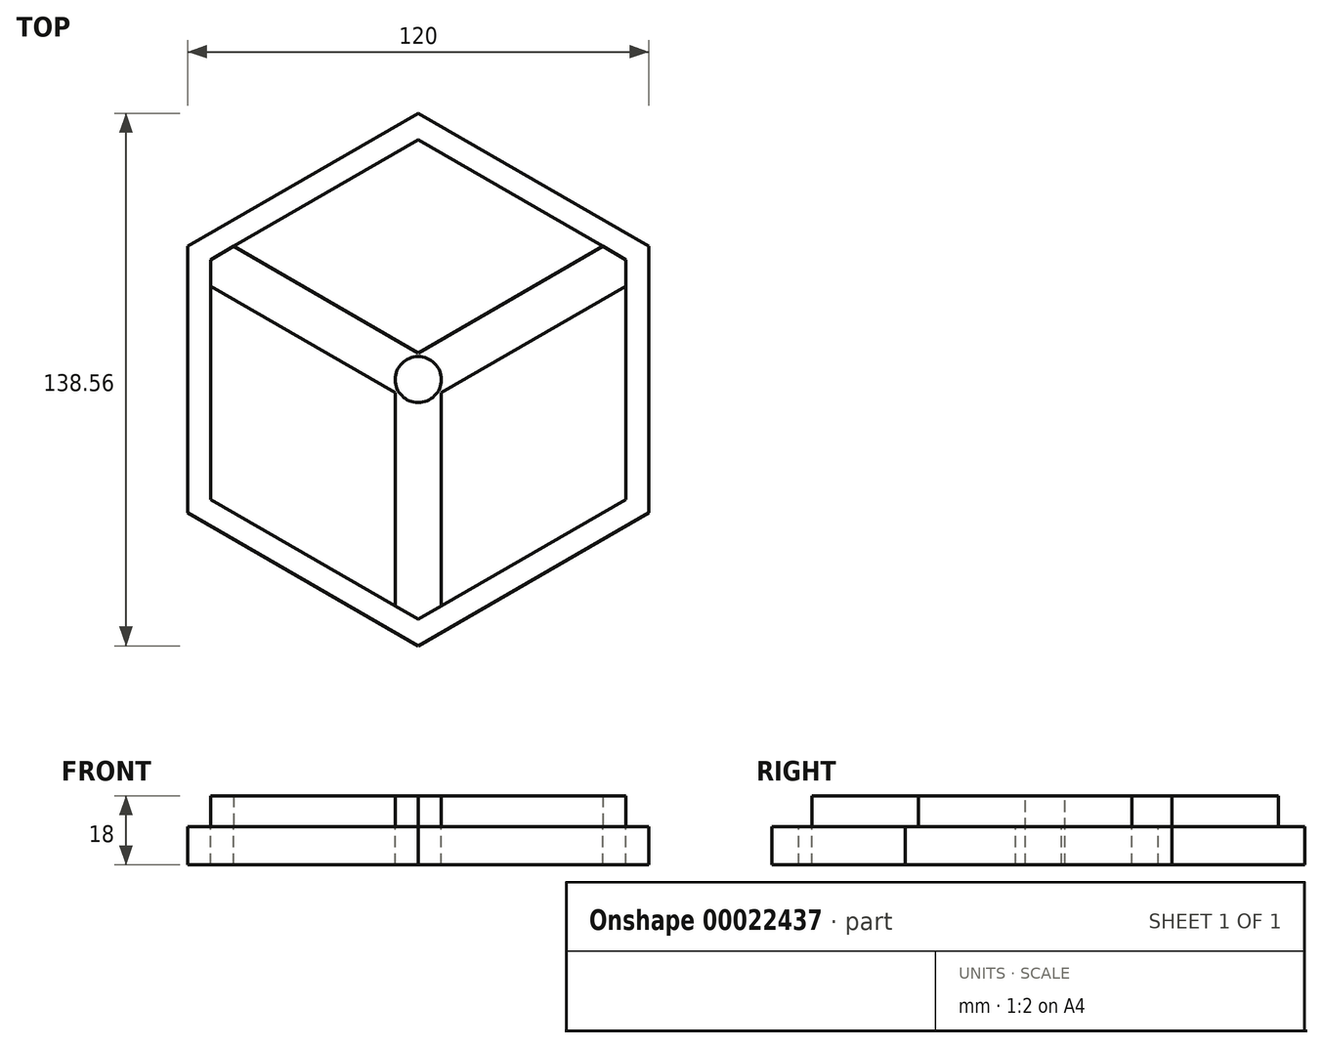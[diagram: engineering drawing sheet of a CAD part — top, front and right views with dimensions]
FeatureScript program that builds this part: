
annotation { "Feature Type Name" : "Feature", "Feature Type Description" : "" }
export const myFeature = defineFeature(function(context is Context, id is Id, definition is map)
    precondition{}
    {
        {
            var Q0;
            Q0=qCreatedBy(makeId("Top.planeOp"),FACE);
            var sketch = newSketch(context, id + "F0", { "sketchPlane" : qUnion([Q0])});
            skCircle(sketch, "E0.cCircle", {"center": v(0, 0) * mm, "radius": 60 * mm, "construction": true});
            skLineSegment(sketch, "E0.0", {"start": v(60, -34.64) * mm, "end": v(0, -69.28) * mm});
            skLineSegment(sketch, "E0.1", {"start": v(0, -69.28) * mm, "end": v(-60, -34.64) * mm});
            skLineSegment(sketch, "E0.2", {"start": v(-60, -34.64) * mm, "end": v(-60, 34.64) * mm});
            skLineSegment(sketch, "E0.3", {"start": v(-60, 34.64) * mm, "end": v(0, 69.28) * mm});
            skLineSegment(sketch, "E0.4", {"start": v(0, 69.28) * mm, "end": v(60, 34.64) * mm});
            skLineSegment(sketch, "E0.5", {"start": v(60, 34.64) * mm, "end": v(60, -34.64) * mm});
            skPoint(sketch, "E0.0.midPoint", {"position": v(30, -51.96) * mm});
            skCircle(sketch, "E1", {"center": v(0, 0) * mm, "radius": 30 * mm, "construction": true});
            skCircle(sketch, "E2", {"center": v(0, -69.28) * mm, "radius": 10 * mm, "construction": true});
            skCircle(sketch, "E3", {"center": v(60, 34.64) * mm, "radius": 10 * mm, "construction": true});
            skCircle(sketch, "E4", {"center": v(-60, 34.64) * mm, "radius": 10 * mm, "construction": true});
            skLineSegment(sketch, "E5.0", {"start": v(-54, -31.18) * mm, "end": v(-54, 31.18) * mm});
            skLineSegment(sketch, "E5.1", {"start": v(0, -62.35) * mm, "end": v(-54, -31.18) * mm});
            skLineSegment(sketch, "E5.2", {"start": v(54, -31.18) * mm, "end": v(0, -62.35) * mm});
            skLineSegment(sketch, "E5.3", {"start": v(54, 31.18) * mm, "end": v(54, -31.18) * mm});
            skLineSegment(sketch, "E5.4", {"start": v(0, 62.35) * mm, "end": v(54, 31.18) * mm});
            skLineSegment(sketch, "E5.5", {"start": v(-54, 31.18) * mm, "end": v(0, 62.35) * mm});
            skLineSegment(sketch, "E6", {"start": v(-54, 31.18) * mm, "end": v(0, 0) * mm});
            skLineSegment(sketch, "E7", {"start": v(0, 0) * mm, "end": v(54, 31.18) * mm});
            skLineSegment(sketch, "E8", {"start": v(0, 0) * mm, "end": v(0, -62.35) * mm});
            skArc(sketch, "E9.0.startCap", {"start": v(-57, 25.98) * mm, "mid": v(-59.2, 34.18) * mm, "end": v(-51, 36.37) * mm});
            skArc(sketch, "E9.0.endCap", {"start": v(3, 5.2) * mm, "mid": v(5.2, -3) * mm, "end": v(-3, -5.2) * mm});
            skLineSegment(sketch, "E9.0.left", {"start": v(-51, 36.37) * mm, "end": v(0, 6.93) * mm});
            skLineSegment(sketch, "E9.0.right", {"start": v(-57, 25.98) * mm, "end": v(-6, -3.46) * mm});
            skArc(sketch, "E9.1.startCap", {"start": v(3, -5.2) * mm, "mid": v(-5.2, -3) * mm, "end": v(-3, 5.2) * mm});
            skArc(sketch, "E9.1.endCap", {"start": v(51, 36.37) * mm, "mid": v(59.2, 34.18) * mm, "end": v(57, 25.98) * mm});
            skLineSegment(sketch, "E9.1.left", {"start": v(0, 6.93) * mm, "end": v(51, 36.37) * mm});
            skLineSegment(sketch, "E9.1.right", {"start": v(6, -3.46) * mm, "end": v(57, 25.98) * mm});
            skArc(sketch, "E9.2.startCap", {"start": v(-6, 0) * mm, "mid": v(0, 6) * mm, "end": v(6, 0) * mm});
            skArc(sketch, "E9.2.endCap", {"start": v(6, -62.35) * mm, "mid": v(0, -68.35) * mm, "end": v(-6, -62.35) * mm});
            skLineSegment(sketch, "E9.2.left", {"start": v(6, -3.46) * mm, "end": v(6, -62.35) * mm});
            skLineSegment(sketch, "E9.2.right", {"start": v(-6, -3.46) * mm, "end": v(-6, -62.35) * mm});
            skLineSegment(sketch, "E10", {"start": v(0, 0) * mm, "end": v(-60, -34.64) * mm, "construction": true});
            skLineSegment(sketch, "E11", {"start": v(0, 0) * mm, "end": v(60, -34.64) * mm, "construction": true});
            skLineSegment(sketch, "E12", {"start": v(-54, 24.25) * mm, "end": v(-6, -58.89) * mm, "construction": true});
            skLineSegment(sketch, "E13", {"start": v(54, 24.25) * mm, "end": v(6, -58.89) * mm, "construction": true});
            skLineSegment(sketch, "E14", {"start": v(-48, 34.64) * mm, "end": v(48, 34.64) * mm, "construction": true});
            skSolve(sketch);
        }
        {
            var Q0;
            Q0 = qSketchRegion(id + "F0", true);
            var Q1;
            {var subQ3=sQuery(id+"F0.wireOp",EDGE,"E9.0.startCap");Q1=makeQuery(id+"F0.imprint","IMPRINT",FACE,{"disambiguationData":[TD([[makeQuery(id+"F0.imprint","IMPRINT",EDGE,{"derivedFrom":subQ3}),-1.0]])]});}
            var Q2;
            {var subQ0=sQuery(id+"F0.wireOp",EDGE,"E9.2.startCap");var subQ2=makeQuery(id+"F0.imprint","IMPRINT",VERTEX,{"disambiguationData":[OD(0.0)],"derivedFrom":subQ0});Q2=makeQuery(id+"F0.imprint","IMPRINT",FACE,{"disambiguationData":[TD([[makeQuery(id+"F0.imprint","IMPRINT",EDGE,{"disambiguationData":[TD([[subQ2,-1.0]])],"derivedFrom":subQ0}),1.0]])]});}
            var Q3;
            {var subQ1=sQuery(id+"F0.wireOp",EDGE,"E5.1");var subQ5=sQuery(id+"F0.wireOp",EDGE,"E5.0");var subQ7=makeQuery(id+"F0.imprint","INTERSECT",VERTEX,{"derivedFrom":[subQ5,subQ1]});Q3=makeQuery(id+"F0.imprint","IMPRINT",FACE,{"disambiguationData":[TD([[makeQuery(id+"F0.imprint","IMPRINT",EDGE,{"disambiguationData":[TD([[subQ7,-1.0]])],"derivedFrom":subQ5}),-1.0]])]});}
            var Q4;
            {var subQ1=sQuery(id+"F0.wireOp",EDGE,"E5.2");var subQ5=sQuery(id+"F0.wireOp",EDGE,"E5.3");var subQ7=makeQuery(id+"F0.imprint","INTERSECT",VERTEX,{"derivedFrom":[subQ1,subQ5]});Q4=makeQuery(id+"F0.imprint","IMPRINT",FACE,{"disambiguationData":[TD([[makeQuery(id+"F0.imprint","IMPRINT",EDGE,{"disambiguationData":[TD([[subQ7,-1.0]])],"derivedFrom":subQ1}),-1.0]])]});}
            var Q5;
            {var subQ1=sQuery(id+"F0.wireOp",EDGE,"E5.4");var subQ5=sQuery(id+"F0.wireOp",EDGE,"E5.5");var subQ7=makeQuery(id+"F0.imprint","INTERSECT",VERTEX,{"derivedFrom":[subQ1,subQ5]});Q5=makeQuery(id+"F0.imprint","IMPRINT",FACE,{"disambiguationData":[TD([[makeQuery(id+"F0.imprint","IMPRINT",EDGE,{"disambiguationData":[TD([[subQ7,-1.0]])],"derivedFrom":subQ1}),-1.0]])]});}
            var Q6;
            {var subQ8=sQuery(id+"F0.wireOp",EDGE,"E9.1.startCap");var subQ12=makeQuery(id+"F0.imprint","IMPRINT",VERTEX,{"derivedFrom":subQ8});Q6=makeQuery(id+"F0.imprint","IMPRINT",FACE,{"disambiguationData":[TD([[makeQuery(id+"F0.imprint","IMPRINT",EDGE,{"disambiguationData":[TD([[subQ12,1.0]])],"derivedFrom":subQ8}),1.0]])]});}
            var Q7;
            {var subQ8=sQuery(id+"F0.wireOp",EDGE,"E9.0.endCap");Q7=makeQuery(id+"F0.imprint","IMPRINT",FACE,{"disambiguationData":[TD([[makeQuery(id+"F0.imprint","IMPRINT",EDGE,{"derivedFrom":subQ8}),1.0]])]});}
            var Q8;
            {var subQ3=sQuery(id+"F0.wireOp",EDGE,"E9.1.endCap");Q8=makeQuery(id+"F0.imprint","IMPRINT",FACE,{"disambiguationData":[TD([[makeQuery(id+"F0.imprint","IMPRINT",EDGE,{"derivedFrom":subQ3}),-1.0]])]});}
            var Q9;
            {var subQ3=sQuery(id+"F0.wireOp",EDGE,"E9.2.endCap");Q9=makeQuery(id+"F0.imprint","IMPRINT",FACE,{"disambiguationData":[TD([[makeQuery(id+"F0.imprint","IMPRINT",EDGE,{"derivedFrom":subQ3}),-1.0]])]});}
            extrude(context, id + "F1", {"entities" : qUnion([Q0, Q1, Q2, Q3, Q4, Q5, Q6, Q7, Q8, Q9]), "oppositeDirection" : true, "depth" : 10 * mm});
        }
        {
            var Q0;
            {var subQ1=sQuery(id+"F0.wireOp",EDGE,"E5.2");var subQ5=sQuery(id+"F0.wireOp",EDGE,"E5.3");var subQ7=makeQuery(id+"F0.imprint","INTERSECT",VERTEX,{"derivedFrom":[subQ1,subQ5]});Q0=makeQuery(id+"F0.imprint","IMPRINT",FACE,{"disambiguationData":[TD([[makeQuery(id+"F0.imprint","IMPRINT",EDGE,{"disambiguationData":[TD([[subQ7,-1.0]])],"derivedFrom":subQ1}),-1.0]])]});}
            var Q1;
            {var subQ1=sQuery(id+"F0.wireOp",EDGE,"E5.4");var subQ5=sQuery(id+"F0.wireOp",EDGE,"E5.5");var subQ7=makeQuery(id+"F0.imprint","INTERSECT",VERTEX,{"derivedFrom":[subQ1,subQ5]});Q1=makeQuery(id+"F0.imprint","IMPRINT",FACE,{"disambiguationData":[TD([[makeQuery(id+"F0.imprint","IMPRINT",EDGE,{"disambiguationData":[TD([[subQ7,-1.0]])],"derivedFrom":subQ1}),-1.0]])]});}
            var Q2;
            {var subQ1=sQuery(id+"F0.wireOp",EDGE,"E5.1");var subQ5=sQuery(id+"F0.wireOp",EDGE,"E5.0");var subQ7=makeQuery(id+"F0.imprint","INTERSECT",VERTEX,{"derivedFrom":[subQ5,subQ1]});Q2=makeQuery(id+"F0.imprint","IMPRINT",FACE,{"disambiguationData":[TD([[makeQuery(id+"F0.imprint","IMPRINT",EDGE,{"disambiguationData":[TD([[subQ7,-1.0]])],"derivedFrom":subQ5}),-1.0]])]});}
            extrude(context, id + "F2", {"entities" : qUnion([Q0, Q1, Q2]), "operationType" : NewBodyOperationType.ADD, "depth" : 8 * mm});
        }
        {
            var Q0;
            {var subQ1=sQuery(id+"F0.wireOp",EDGE,"E5.4");var subQ5=sQuery(id+"F0.wireOp",EDGE,"E5.5");var subQ7=makeQuery(id+"F0.imprint","INTERSECT",VERTEX,{"derivedFrom":[subQ1,subQ5]});Q0=makeQuery(id+"F0.imprint","IMPRINT",FACE,{"disambiguationData":[TD([[makeQuery(id+"F0.imprint","IMPRINT",EDGE,{"disambiguationData":[TD([[subQ7,-1.0]])],"derivedFrom":subQ1}),-1.0]])]});}
            var Q1;
            {var subQ1=sQuery(id+"F0.wireOp",EDGE,"E5.1");var subQ5=sQuery(id+"F0.wireOp",EDGE,"E5.0");var subQ7=makeQuery(id+"F0.imprint","INTERSECT",VERTEX,{"derivedFrom":[subQ5,subQ1]});Q1=makeQuery(id+"F0.imprint","IMPRINT",FACE,{"disambiguationData":[TD([[makeQuery(id+"F0.imprint","IMPRINT",EDGE,{"disambiguationData":[TD([[subQ7,-1.0]])],"derivedFrom":subQ5}),-1.0]])]});}
            var Q2;
            {var subQ1=sQuery(id+"F0.wireOp",EDGE,"E5.2");var subQ5=sQuery(id+"F0.wireOp",EDGE,"E5.3");var subQ7=makeQuery(id+"F0.imprint","INTERSECT",VERTEX,{"derivedFrom":[subQ1,subQ5]});Q2=makeQuery(id+"F0.imprint","IMPRINT",FACE,{"disambiguationData":[TD([[makeQuery(id+"F0.imprint","IMPRINT",EDGE,{"disambiguationData":[TD([[subQ7,-1.0]])],"derivedFrom":subQ1}),-1.0]])]});}
            extrude(context, id + "F3", {"entities" : qUnion([Q0, Q1, Q2]), "oppositeDirection" : true, "depth" : 25 * mm});
        }
        {
            var Q0;
            Q0=makeQuery(id+"F3.opExtrude","SWEPT_BODY",BODY,{"disambiguationData":[OSD([sQuery(id+"F0.wireOp",EDGE,"E5.4"),sQuery(id+"F0.wireOp",EDGE,"E5.5"),sQuery(id+"F0.wireOp",EDGE,"E9.0.left"),sQuery(id+"F0.wireOp",EDGE,"E9.1.left")])]});
            var Q1;
            Q1=makeQuery(id+"F3.opExtrude","SWEPT_BODY",BODY,{"disambiguationData":[OSD([sQuery(id+"F0.wireOp",EDGE,"E5.0"),sQuery(id+"F0.wireOp",EDGE,"E5.1"),sQuery(id+"F0.wireOp",EDGE,"E9.0.right"),sQuery(id+"F0.wireOp",EDGE,"E9.2.right")])]});
            var Q2;
            Q2=makeQuery(id+"F3.opExtrude","SWEPT_BODY",BODY,{"disambiguationData":[OSD([sQuery(id+"F0.wireOp",EDGE,"E5.2"),sQuery(id+"F0.wireOp",EDGE,"E5.3"),sQuery(id+"F0.wireOp",EDGE,"E9.1.right"),sQuery(id+"F0.wireOp",EDGE,"E9.2.left")])]});
            var Q3;
            Q3=makeQuery(id+"F3.opExtrude","SWEPT_EDGE",EDGE,{"disambiguationData":[OSD([sQuery(id+"F0.wireOp",EDGE,"E5.3"),sQuery(id+"F0.wireOp",EDGE,"E9.1.right")])]});
            transform(context, id + "F4", {"entities" : qUnion([Q0, Q1, Q2]), "transformType" : TransformType.TRANSLATION_DISTANCE, "transformDirection" : qUnion([Q3]), "distance" : 2 * mm, "oppositeDirection" : true, "makeCopy" : false});
        }
        {
            var Q0;
            Q0=makeQuery(id+"F3.opExtrude","SWEPT_BODY",BODY,{"disambiguationData":[OSD([sQuery(id+"F0.wireOp",EDGE,"E5.4"),sQuery(id+"F0.wireOp",EDGE,"E5.5"),sQuery(id+"F0.wireOp",EDGE,"E9.0.left"),sQuery(id+"F0.wireOp",EDGE,"E9.1.left")])]});
            var Q1;
            Q1=makeQuery(id+"F3.opExtrude","SWEPT_BODY",BODY,{"disambiguationData":[OSD([sQuery(id+"F0.wireOp",EDGE,"E5.2"),sQuery(id+"F0.wireOp",EDGE,"E5.3"),sQuery(id+"F0.wireOp",EDGE,"E9.1.right"),sQuery(id+"F0.wireOp",EDGE,"E9.2.left")])]});
            var Q2;
            Q2=makeQuery(id+"F3.opExtrude","SWEPT_BODY",BODY,{"disambiguationData":[OSD([sQuery(id+"F0.wireOp",EDGE,"E5.0"),sQuery(id+"F0.wireOp",EDGE,"E5.1"),sQuery(id+"F0.wireOp",EDGE,"E9.0.right"),sQuery(id+"F0.wireOp",EDGE,"E9.2.right")])]});
            var Q3;
            Q3=makeQuery(id+"F1.opExtrude","SWEPT_BODY",BODY,{"disambiguationData":[OSD([sQuery(id+"F0.wireOp",EDGE,"E0.0"),sQuery(id+"F0.wireOp",EDGE,"E0.1"),sQuery(id+"F0.wireOp",EDGE,"E0.2"),sQuery(id+"F0.wireOp",EDGE,"E0.3"),sQuery(id+"F0.wireOp",EDGE,"E0.4"),sQuery(id+"F0.wireOp",EDGE,"E0.5"),sQuery(id+"F0.wireOp",EDGE,"E9.0.endCap"),sQuery(id+"F0.wireOp",EDGE,"E9.1.startCap"),sQuery(id+"F0.wireOp",EDGE,"E9.2.startCap")])]});
            booleanBodies(context, id + "F5", {"operationType" : BooleanOperationType.SUBTRACTION, "tools" : qUnion([Q0, Q1, Q2]), "targets" : qUnion([Q3])});
        }
    });
